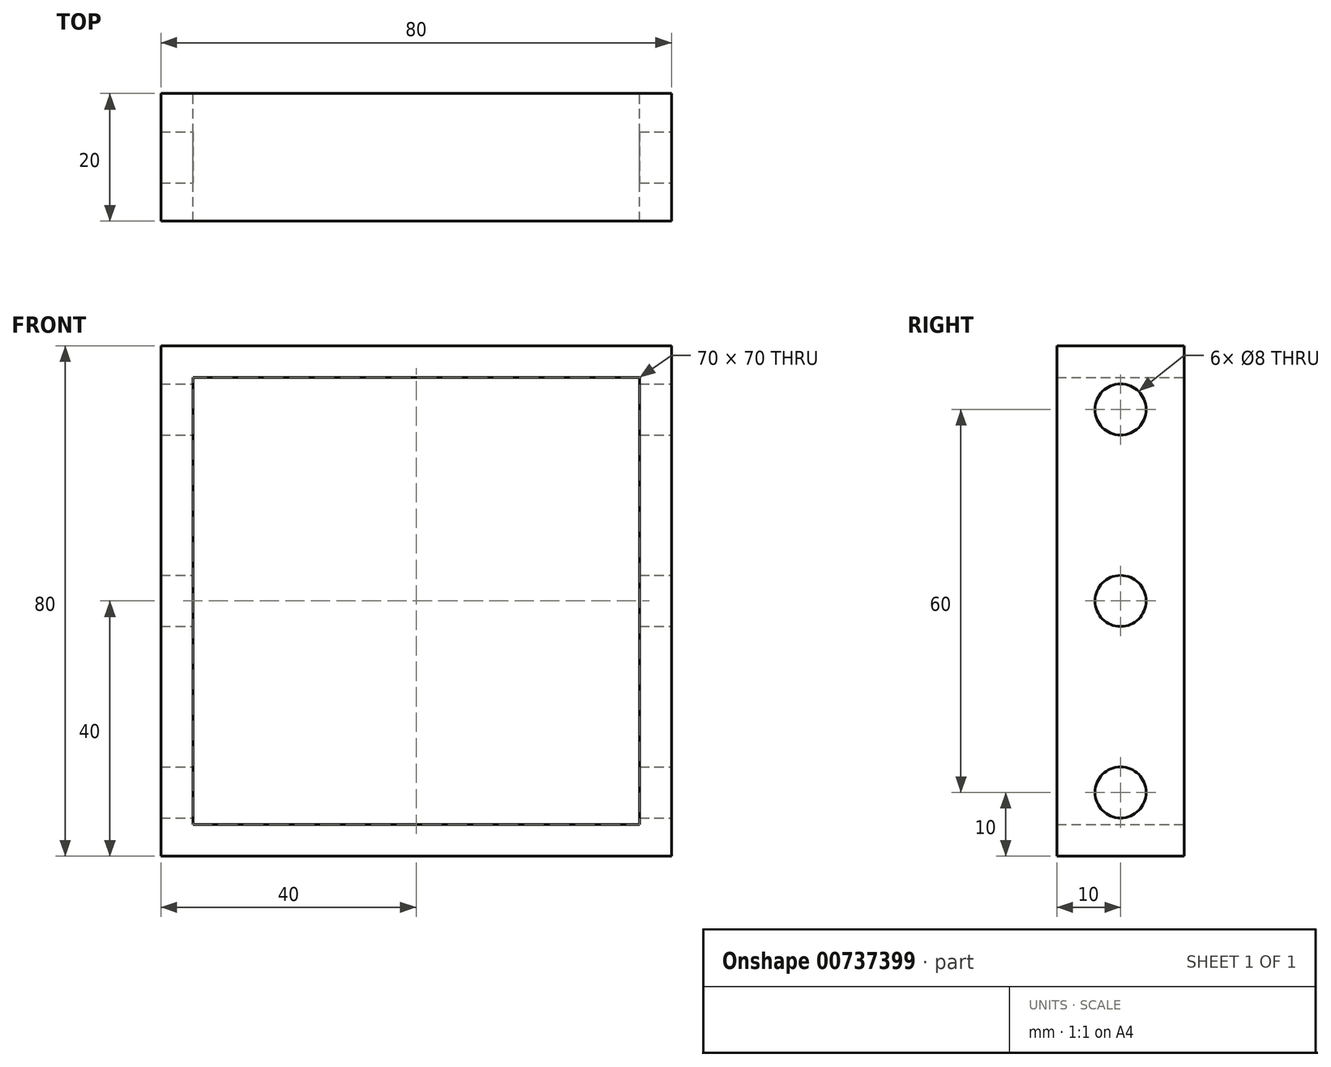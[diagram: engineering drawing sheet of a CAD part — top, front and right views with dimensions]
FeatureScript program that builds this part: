
annotation { "Feature Type Name" : "Feature", "Feature Type Description" : "" }
export const myFeature = defineFeature(function(context is Context, id is Id, definition is map)
    precondition{}
    {
        {
            var Q0;
            Q0=qCreatedBy(makeId("Front.planeOp"),FACE);
            var sketch = newSketch(context, id + "F0", { "sketchPlane" : qUnion([Q0])});
            skLineSegment(sketch, "E0.bottom", {"start": v(40, 40) * mm, "end": v(-40, 40) * mm});
            skLineSegment(sketch, "E0.top", {"start": v(40, -40) * mm, "end": v(-40, -40) * mm});
            skLineSegment(sketch, "E0.left", {"start": v(40, 40) * mm, "end": v(40, -40) * mm});
            skLineSegment(sketch, "E0.right", {"start": v(-40, 40) * mm, "end": v(-40, -40) * mm});
            skPoint(sketch, "E0.middle", {"position": v(0, 0) * mm});
            skLineSegment(sketch, "E1.bottom", {"start": v(35, 35) * mm, "end": v(-35, 35) * mm});
            skLineSegment(sketch, "E1.top", {"start": v(35, -35) * mm, "end": v(-35, -35) * mm});
            skLineSegment(sketch, "E1.left", {"start": v(35, 35) * mm, "end": v(35, -35) * mm});
            skLineSegment(sketch, "E1.right", {"start": v(-35, 35) * mm, "end": v(-35, -35) * mm});
            skSolve(sketch);
        }
        {
            var Q0;
            Q0=makeQuery(id+"F0.imprint","IMPRINT",FACE,{"disambiguationData":[TD([[makeQuery(id+"F0.imprint","IMPRINT",EDGE,{"derivedFrom":sQuery(id+"F0.wireOp",EDGE,"E0.bottom")}),1.0]])]});
            extrude(context, id + "F1", {"entities" : qUnion([Q0]), "depth" : 20 * mm, "offsetDistance" : 25 * mm});
        }
        {
            var Q0;
            Q0=makeQuery(id+"F1.opExtrude","SWEPT_FACE",FACE,{"disambiguationData":[OSD([sQuery(id+"F0.wireOp",EDGE,"E0.left")])]});
            var sketch = newSketch(context, id + "F2", { "sketchPlane" : qUnion([Q0])});
            skCircle(sketch, "E2", {"center": v(-10, 30) * mm, "radius": 4 * mm});
            skPoint(sketch, "E2.centerSnap0", {"position": v(-10, 40) * mm});
            skCircle(sketch, "E3", {"center": v(-10, 0) * mm, "radius": 4 * mm});
            skCircle(sketch, "E4", {"center": v(-10, -30) * mm, "radius": 4 * mm});
            skSolve(sketch);
        }
        {
            var Q0;
            Q0=makeQuery(id+"F2.imprint","IMPRINT",FACE,{"disambiguationData":[TD([[makeQuery(id+"F2.imprint","IMPRINT",EDGE,{"derivedFrom":sQuery(id+"F2.wireOp",EDGE,"E2")}),1.0]])]});
            var Q1;
            Q1=makeQuery(id+"F2.imprint","IMPRINT",FACE,{"disambiguationData":[TD([[makeQuery(id+"F2.imprint","IMPRINT",EDGE,{"derivedFrom":sQuery(id+"F2.wireOp",EDGE,"E3")}),1.0]])]});
            var Q2;
            Q2=makeQuery(id+"F2.imprint","IMPRINT",FACE,{"disambiguationData":[TD([[makeQuery(id+"F2.imprint","IMPRINT",EDGE,{"derivedFrom":sQuery(id+"F2.wireOp",EDGE,"E4")}),1.0]])]});
            extrude(context, id + "F3", {"entities" : qUnion([Q0, Q1, Q2]), "operationType" : NewBodyOperationType.REMOVE, "endBound" : BoundingType.THROUGH_ALL, "oppositeDirection" : true, "depth" : 25 * mm, "offsetDistance" : 25 * mm});
        }
    });
